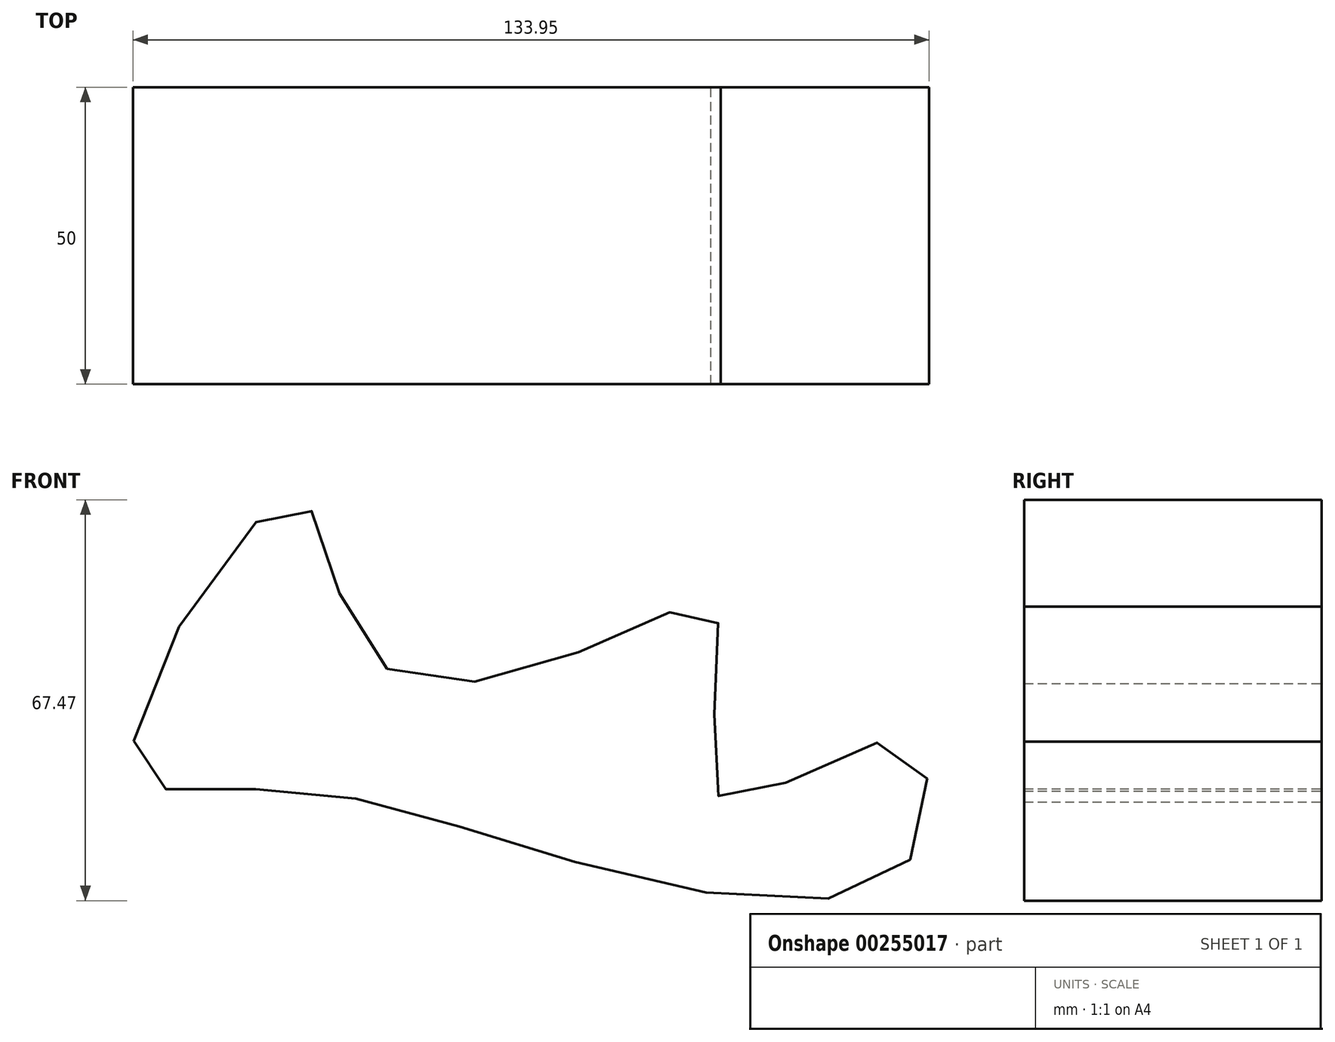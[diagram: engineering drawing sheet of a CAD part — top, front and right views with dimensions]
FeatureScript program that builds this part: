
annotation { "Feature Type Name" : "Feature", "Feature Type Description" : "" }
export const myFeature = defineFeature(function(context is Context, id is Id, definition is map)
    precondition{}
    {
        {
            var Q0;
            Q0=qCreatedBy(makeId("Front.planeOp"),FACE);
            var sketch = newSketch(context, id + "F0", { "sketchPlane" : qUnion([Q0])});
            skFitSpline(sketch, "E0", {"points": [v(0, 35.48) * mm, v(23.27, 41.1) * mm, v(24.1, 10.78) * mm, v(53.66, 20.29) * mm, v(55.36, 0) * mm, v(0, 0) * mm, v(-51.5, 12.46) * mm, v(-74.83, 17.25) * mm, v(-47.96, 61.12) * mm, v(-35.87, 36.02) * mm, v(0, 35.48) * mm]});
            skSolve(sketch);
        }
        {
            var Q0;
            Q0 = qSketchRegion(id + "F0", true);
            extrude(context, id + "F1", {"entities" : qUnion([Q0]), "depth" : 50 * mm});
        }
    });
